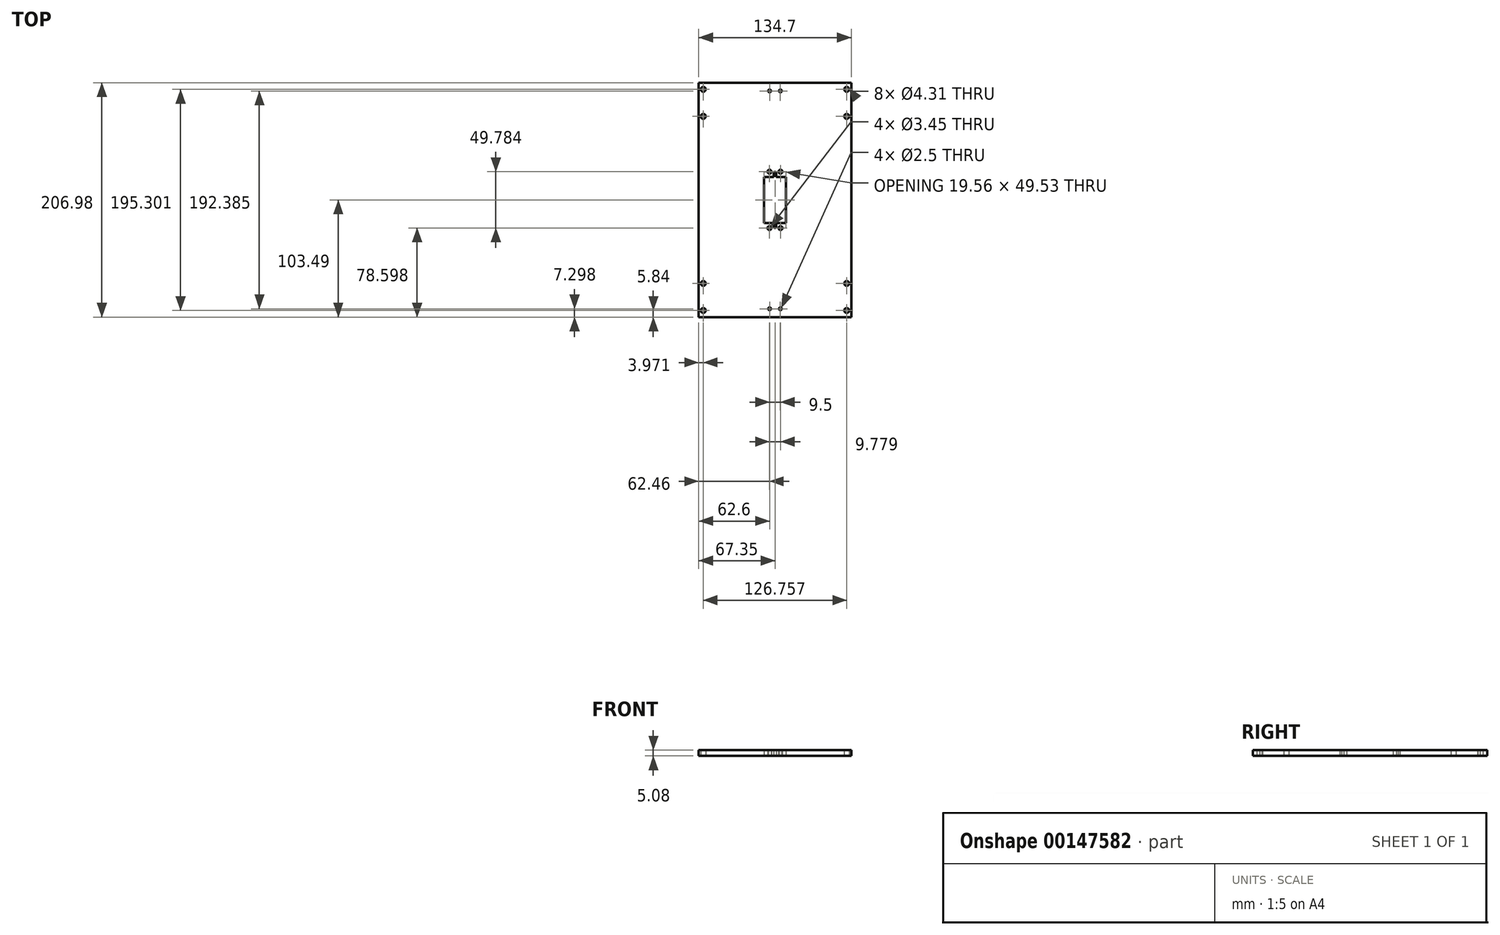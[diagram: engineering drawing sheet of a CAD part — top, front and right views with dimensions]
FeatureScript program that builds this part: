
annotation { "Feature Type Name" : "Feature", "Feature Type Description" : "" }
export const myFeature = defineFeature(function(context is Context, id is Id, definition is map)
    precondition{}
    {
        {
            var Q0;
            Q0=qCreatedBy(makeId("Top.planeOp"),FACE);
            var sketch = newSketch(context, id + "F0", { "sketchPlane" : qUnion([Q0])});
            skLineSegment(sketch, "E0.rect.bottom", {"start": v(-9.78, -20.32) * mm, "end": v(-9.78, 20.32) * mm});
            skLineSegment(sketch, "E0.rect.top", {"start": v(9.78, -20.32) * mm, "end": v(9.78, 20.32) * mm});
            skPoint(sketch, "E0.rect.middle", {"position": v(0, 0) * mm});
            skLineSegment(sketch, "E1.rect.bottom", {"start": v(-4.89, -24.9) * mm, "end": v(-4.89, 24.9) * mm, "construction": true});
            skLineSegment(sketch, "E1.rect.top", {"start": v(4.89, -24.9) * mm, "end": v(4.89, 24.9) * mm, "construction": true});
            skLineSegment(sketch, "E1.rect.left", {"start": v(-4.89, -24.9) * mm, "end": v(4.89, -24.9) * mm, "construction": true});
            skLineSegment(sketch, "E1.rect.right", {"start": v(-4.89, 24.9) * mm, "end": v(4.89, 24.9) * mm, "construction": true});
            skCircle(sketch, "E2", {"center": v(4.89, 24.9) * mm, "radius": 1.73 * mm});
            skCircle(sketch, "E3", {"center": v(-4.89, 24.9) * mm, "radius": 1.73 * mm});
            skCircle(sketch, "E4", {"center": v(4.89, -24.9) * mm, "radius": 1.73 * mm});
            skCircle(sketch, "E5", {"center": v(-4.89, -24.9) * mm, "radius": 1.73 * mm});
            skLineSegment(sketch, "E6", {"start": v(-9.78, 20.32) * mm, "end": v(-1.02, 20.32) * mm});
            skLineSegment(sketch, "E7", {"start": v(-1.02, 20.32) * mm, "end": v(-1.02, 23.75) * mm});
            skLineSegment(sketch, "E8", {"start": v(-1.02, 23.75) * mm, "end": v(1.02, 23.75) * mm, "construction": true});
            skLineSegment(sketch, "E9", {"start": v(1.02, 23.75) * mm, "end": v(1.02, 20.32) * mm});
            skLineSegment(sketch, "E10", {"start": v(1.02, 20.32) * mm, "end": v(9.78, 20.32) * mm});
            skLineSegment(sketch, "E11", {"start": v(9.78, -20.32) * mm, "end": v(1.02, -20.32) * mm});
            skLineSegment(sketch, "E12", {"start": v(1.02, -20.32) * mm, "end": v(1.02, -23.75) * mm});
            skLineSegment(sketch, "E13", {"start": v(1.02, -23.75) * mm, "end": v(-1.02, -23.75) * mm, "construction": true});
            skLineSegment(sketch, "E14", {"start": v(-1.02, -23.75) * mm, "end": v(-1.02, -20.32) * mm});
            skLineSegment(sketch, "E15", {"start": v(-1.02, -20.32) * mm, "end": v(-9.78, -20.32) * mm});
            skArc(sketch, "E16", {"start": v(1.02, 23.75) * mm, "mid": v(0, 24.77) * mm, "end": v(-1.02, 23.75) * mm});
            skArc(sketch, "E17", {"start": v(-1.02, -23.75) * mm, "mid": v(0, -24.76) * mm, "end": v(1.02, -23.75) * mm});
            skLineSegment(sketch, "E18", {"start": v(-1.02, 20.32) * mm, "end": v(1.02, 20.32) * mm, "construction": true});
            skLineSegment(sketch, "E19", {"start": v(0, 20.32) * mm, "end": v(0, 10.9) * mm, "construction": true});
            skLineSegment(sketch, "E20.bottom", {"start": v(67.35, -103.5) * mm, "end": v(-67.35, -103.5) * mm});
            skLineSegment(sketch, "E20.top", {"start": v(67.35, 103.5) * mm, "end": v(-67.35, 103.5) * mm});
            skLineSegment(sketch, "E20.left", {"start": v(67.35, -103.5) * mm, "end": v(67.35, 103.5) * mm});
            skLineSegment(sketch, "E20.right", {"start": v(-67.35, -103.5) * mm, "end": v(-67.35, 103.5) * mm});
            skLineSegment(sketch, "E21", {"start": v(0, 0) * mm, "end": v(0, 0) * mm});
            skLineSegment(sketch, "E22.bottom", {"start": v(-63.38, 73.77) * mm, "end": v(63.38, 73.77) * mm, "construction": true});
            skLineSegment(sketch, "E22.top", {"start": v(-63.38, -73.77) * mm, "end": v(63.38, -73.77) * mm, "construction": true});
            skLineSegment(sketch, "E22.left", {"start": v(-63.38, 73.77) * mm, "end": v(-63.38, -73.77) * mm, "construction": true});
            skLineSegment(sketch, "E22.right", {"start": v(63.38, 73.77) * mm, "end": v(63.38, -73.77) * mm, "construction": true});
            skCircle(sketch, "E23", {"center": v(-63.38, 73.77) * mm, "radius": 2.15 * mm});
            skCircle(sketch, "E24", {"center": v(63.38, 73.77) * mm, "radius": 2.15 * mm});
            skCircle(sketch, "E25", {"center": v(-63.38, -73.77) * mm, "radius": 2.15 * mm});
            skCircle(sketch, "E26", {"center": v(63.38, -73.77) * mm, "radius": 2.15 * mm});
            skLineSegment(sketch, "E27", {"start": v(63.38, 73.77) * mm, "end": v(63.38, 97.65) * mm, "construction": true});
            skLineSegment(sketch, "E28", {"start": v(-63.38, 73.77) * mm, "end": v(-63.38, 97.65) * mm, "construction": true});
            skLineSegment(sketch, "E29", {"start": v(-63.38, -73.77) * mm, "end": v(-63.38, -97.65) * mm, "construction": true});
            skLineSegment(sketch, "E30", {"start": v(63.38, -73.77) * mm, "end": v(63.38, -97.65) * mm, "construction": true});
            skCircle(sketch, "E31", {"center": v(-63.38, 97.65) * mm, "radius": 2.15 * mm});
            skCircle(sketch, "E32", {"center": v(63.38, 97.65) * mm, "radius": 2.15 * mm});
            skCircle(sketch, "E33", {"center": v(63.38, -97.65) * mm, "radius": 2.15 * mm});
            skCircle(sketch, "E34", {"center": v(-63.38, -97.65) * mm, "radius": 2.15 * mm});
            skLineSegment(sketch, "E35", {"start": v(63.38, 97.65) * mm, "end": v(63.38, 103.5) * mm, "construction": true});
            skLineSegment(sketch, "E36", {"start": v(63.38, 97.65) * mm, "end": v(67.35, 97.65) * mm, "construction": true});
            skLineSegment(sketch, "E37", {"start": v(-63.38, -97.65) * mm, "end": v(-63.38, -103.5) * mm, "construction": true});
            skLineSegment(sketch, "E38", {"start": v(-63.38, -97.65) * mm, "end": v(-67.35, -97.65) * mm, "construction": true});
            skLineSegment(sketch, "E39", {"start": v(0, -103.5) * mm, "end": v(0, -96.2) * mm, "construction": true});
            skLineSegment(sketch, "E40", {"start": v(-4.75, -96.2) * mm, "end": v(4.75, -96.2) * mm, "construction": true});
            skLineSegment(sketch, "E41", {"start": v(0, 103.5) * mm, "end": v(0, 96.2) * mm, "construction": true});
            skLineSegment(sketch, "E42", {"start": v(-4.75, 96.2) * mm, "end": v(4.75, 96.2) * mm, "construction": true});
            skCircle(sketch, "E43", {"center": v(-4.75, -96.2) * mm, "radius": 1.25 * mm});
            skCircle(sketch, "E44", {"center": v(4.75, -96.2) * mm, "radius": 1.25 * mm});
            skCircle(sketch, "E45", {"center": v(-4.75, 96.2) * mm, "radius": 1.25 * mm});
            skCircle(sketch, "E46", {"center": v(4.75, 96.2) * mm, "radius": 1.25 * mm});
            skSolve(sketch);
        }
        {
            var Q0;
            Q0=qSketchRegion(id+"F0",true);
            extrude(context, id + "F1", {"entities" : qUnion([Q0]), "depth" : 5.08 * mm});
        }
    });
